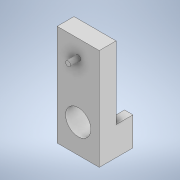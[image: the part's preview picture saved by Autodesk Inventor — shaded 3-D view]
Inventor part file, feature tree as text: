
AUTODESK INVENTOR PART (.ipt)
format: ipt  version: 2021 (Build 250183000, 183)  size: 327,680 bytes
history: native  units: mm
features: sketch x5, extrude x4, thread x1, emboss x1
ambient origin geometry x8: Origin, YZ Plane, XZ Plane, XY Plane, X Axis, Y Axis, Z Axis, Center Point
bodies: Solid1 (feature_tree)
feature tree (11):
  extrude  "Extrusion1"  Depth=25.0mm
  extrude  "Extrusion2"  Depth=12.5mm
  thread  "Thread1"  [1 undecoded]
  extrude  "Extrusion3"  Depth=6.0mm TaperAngle=0.0deg
  extrude  "Extrusion5"  Depth=10.0mm TaperAngle=0.0deg
  emboss  "Emboss1"
  sketch  "Sketch1"  dims[d0=60.0mm d1=25.0mm]
  sketch  "Sketch2"  dims[d2=12.5mm d5=12.5mm d6=10.0mm d7=0.0mm]
  sketch  "Sketch3"  dims[d8=3.0mm d10=6.0mm d11=0.0mm]
  sketch  "Sketch5"  dims[d12=6.0mm d13=0.0mm d15=10.0mm d16=0.0mm]
  sketch  "Sketch6"  dims[d20=17.0mm d21=5.0mm d22=5.0mm d25=7.5mm d26=15.0mm d27=10.0mm d28=0.0mm d29=37.5mm d30=1.0mm d31=0.0mm d9=0.872665mm]
note: 1 required parameter value undecoded (feature->parameter linkage not recoverable at this tier; creation-order binding heuristic only, values carry confidence <= 0.55)
